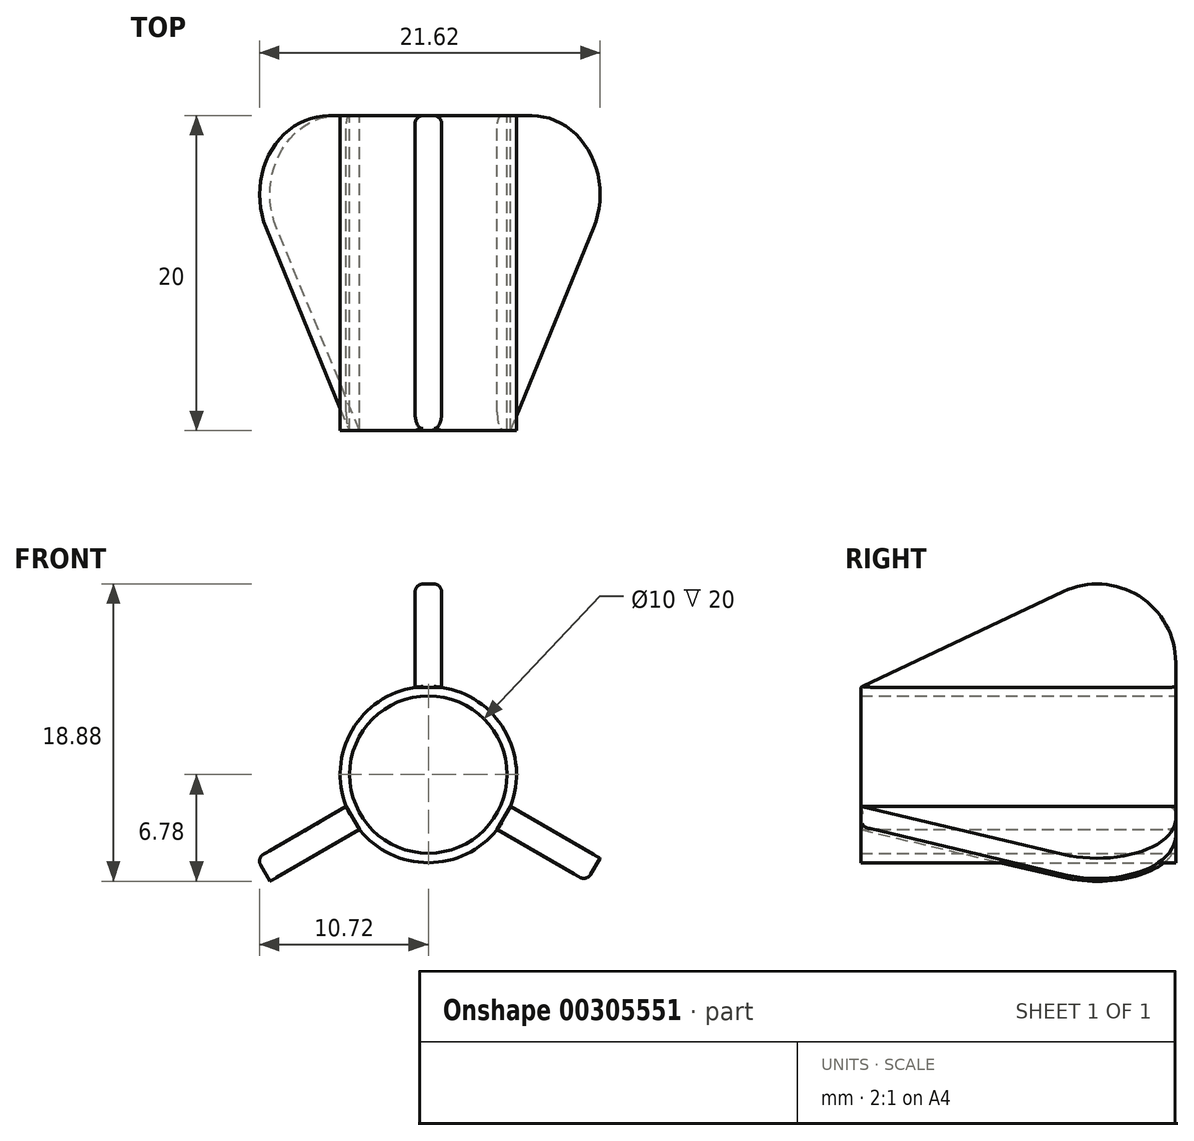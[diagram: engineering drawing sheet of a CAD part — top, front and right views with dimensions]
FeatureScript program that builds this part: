
annotation { "Feature Type Name" : "Feature", "Feature Type Description" : "" }
export const myFeature = defineFeature(function(context is Context, id is Id, definition is map)
    precondition{}
    {
        {
            var Q0;
            Q0=qCreatedBy(makeId("Front.planeOp"),FACE);
            var sketch = newSketch(context, id + "F0", { "sketchPlane" : qUnion([Q0])});
            skCircle(sketch, "E0", {"center": v(0, 0) * mm, "radius": 5 * mm});
            skCircle(sketch, "E1.0", {"center": v(0, 0) * mm, "radius": 5.6 * mm});
            skLineSegment(sketch, "E2.bottom", {"start": v(0, 5) * mm, "end": v(0.85, 5) * mm});
            skLineSegment(sketch, "E2.top", {"start": v(0, 15) * mm, "end": v(0.85, 15) * mm});
            skLineSegment(sketch, "E2.left", {"start": v(0, 5) * mm, "end": v(0, 15) * mm});
            skLineSegment(sketch, "E2.right", {"start": v(0.85, 5) * mm, "end": v(0.85, 15) * mm});
            skLineSegment(sketch, "E3.MirrorCS", {"start": v(0, 15) * mm, "end": v(-0.85, 15) * mm});
            skLineSegment(sketch, "E4.MirrorCS", {"start": v(0, 5) * mm, "end": v(-0.85, 5) * mm});
            skLineSegment(sketch, "E5.MirrorCS", {"start": v(-0.85, 5) * mm, "end": v(-0.85, 15) * mm});
            skLineSegment(sketch, "E6.1.0", {"start": v(-3.9, -3.23) * mm, "end": v(-12.57, -8.23) * mm});
            skLineSegment(sketch, "E6.1.1", {"start": v(-4.75, -1.77) * mm, "end": v(-13.41, -6.77) * mm});
            skLineSegment(sketch, "E6.1.2", {"start": v(-4.33, -2.5) * mm, "end": v(-13, -7.5) * mm});
            skLineSegment(sketch, "E6.1.3", {"start": v(-4.33, -2.5) * mm, "end": v(-3.9, -3.23) * mm});
            skLineSegment(sketch, "E6.1.4", {"start": v(-13, -7.5) * mm, "end": v(-12.57, -8.23) * mm});
            skLineSegment(sketch, "E6.1.5", {"start": v(-13, -7.5) * mm, "end": v(-13.41, -6.77) * mm});
            skLineSegment(sketch, "E6.1.6", {"start": v(-4.33, -2.5) * mm, "end": v(-4.75, -1.77) * mm});
            skLineSegment(sketch, "E6.2.0", {"start": v(4.75, -1.77) * mm, "end": v(13.41, -6.77) * mm});
            skLineSegment(sketch, "E6.2.1", {"start": v(3.9, -3.23) * mm, "end": v(12.57, -8.23) * mm});
            skLineSegment(sketch, "E6.2.2", {"start": v(4.33, -2.5) * mm, "end": v(13, -7.5) * mm});
            skLineSegment(sketch, "E6.2.3", {"start": v(4.33, -2.5) * mm, "end": v(4.75, -1.77) * mm});
            skLineSegment(sketch, "E6.2.4", {"start": v(13, -7.5) * mm, "end": v(13.41, -6.77) * mm});
            skLineSegment(sketch, "E6.2.5", {"start": v(13, -7.5) * mm, "end": v(12.57, -8.23) * mm});
            skLineSegment(sketch, "E6.2.6", {"start": v(4.33, -2.5) * mm, "end": v(3.9, -3.23) * mm});
            skSolve(sketch);
        }
        {
            var Q0;
            {var subQ0=sQuery(id+"F0.wireOp",EDGE,"E4.MirrorCS");Q0=makeQuery(id+"F0.imprint","IMPRINT",FACE,{"disambiguationData":[TD([[makeQuery(id+"F0.imprint","IMPRINT",EDGE,{"derivedFrom":subQ0}),1.0]])]});}
            var Q1;
            {var subQ0=sQuery(id+"F0.wireOp",EDGE,"E6.1.3");Q1=makeQuery(id+"F0.imprint","IMPRINT",FACE,{"disambiguationData":[TD([[makeQuery(id+"F0.imprint","IMPRINT",EDGE,{"derivedFrom":subQ0}),1.0]])]});}
            var Q2;
            {var subQ5=sQuery(id+"F0.wireOp",EDGE,"E6.1.3");Q2=makeQuery(id+"F0.imprint","IMPRINT",FACE,{"disambiguationData":[TD([[makeQuery(id+"F0.imprint","IMPRINT",EDGE,{"derivedFrom":subQ5}),-1.0]])]});}
            var Q3;
            {var subQ5=sQuery(id+"F0.wireOp",EDGE,"E6.1.6");Q3=makeQuery(id+"F0.imprint","IMPRINT",FACE,{"disambiguationData":[TD([[makeQuery(id+"F0.imprint","IMPRINT",EDGE,{"derivedFrom":subQ5}),1.0]])]});}
            var Q4;
            {var subQ5=sQuery(id+"F0.wireOp",EDGE,"E6.2.6");Q4=makeQuery(id+"F0.imprint","IMPRINT",FACE,{"disambiguationData":[TD([[makeQuery(id+"F0.imprint","IMPRINT",EDGE,{"derivedFrom":subQ5}),1.0]])]});}
            var Q5;
            {var subQ5=sQuery(id+"F0.wireOp",EDGE,"E6.2.3");Q5=makeQuery(id+"F0.imprint","IMPRINT",FACE,{"disambiguationData":[TD([[makeQuery(id+"F0.imprint","IMPRINT",EDGE,{"derivedFrom":subQ5}),-1.0]])]});}
            var Q6;
            {var subQ1=sQuery(id+"F0.wireOp",EDGE,"E2.bottom");Q6=makeQuery(id+"F0.imprint","IMPRINT",FACE,{"disambiguationData":[TD([[makeQuery(id+"F0.imprint","IMPRINT",EDGE,{"derivedFrom":subQ1}),-1.0]])]});}
            var Q7;
            {var subQ5=sQuery(id+"F0.wireOp",EDGE,"E2.bottom");Q7=makeQuery(id+"F0.imprint","IMPRINT",FACE,{"disambiguationData":[TD([[makeQuery(id+"F0.imprint","IMPRINT",EDGE,{"derivedFrom":subQ5}),1.0]])]});}
            var Q8;
            {var subQ5=sQuery(id+"F0.wireOp",EDGE,"E4.MirrorCS");Q8=makeQuery(id+"F0.imprint","IMPRINT",FACE,{"disambiguationData":[TD([[makeQuery(id+"F0.imprint","IMPRINT",EDGE,{"derivedFrom":subQ5}),-1.0]])]});}
            extrude(context, id + "F1", {"entities" : qUnion([Q0, Q1, Q2, Q3, Q4, Q5, Q6, Q7, Q8]), "depth" : 20 * mm});
        }
        {
            var Q0;
            {var subQ5=sQuery(id+"F0.wireOp",EDGE,"E6.1.4");Q0=makeQuery(id+"F0.imprint","IMPRINT",FACE,{"disambiguationData":[TD([[makeQuery(id+"F0.imprint","IMPRINT",EDGE,{"derivedFrom":subQ5}),1.0]])]});}
            var Q1;
            {var subQ5=sQuery(id+"F0.wireOp",EDGE,"E6.1.5");Q1=makeQuery(id+"F0.imprint","IMPRINT",FACE,{"disambiguationData":[TD([[makeQuery(id+"F0.imprint","IMPRINT",EDGE,{"derivedFrom":subQ5}),-1.0]])]});}
            extrude(context, id + "F2", {"entities" : qUnion([Q0, Q1]), "operationType" : NewBodyOperationType.ADD, "depth" : 20 * mm});
        }
        {
            var Q0;
            Q0=makeQuery(id+"F2.opExtrude","SWEPT_FACE",FACE,{"disambiguationData":[OSD([sQuery(id+"F0.wireOp",EDGE,"E6.1.0")])]});
            var sketch = newSketch(context, id + "F3", { "sketchPlane" : qUnion([Q0])});
            skLineSegment(sketch, "E7", {"start": v(-5.54, 20) * mm, "end": v(-15, 0) * mm});
            skSolve(sketch);
        }
        {
            var Q0;
            Q0=makeQuery(id+"F3.imprint","IMPRINT",FACE,{"disambiguationData":[TD([[makeQuery(id+"F3.imprint","IMPRINT",EDGE,{"derivedFrom":sQuery(id+"F3.wireOp",EDGE,"E7")}),-1.0]])]});
            extrude(context, id + "F4", {"entities" : qUnion([Q0]), "operationType" : NewBodyOperationType.REMOVE, "oppositeDirection" : true, "depth" : 14.8 * mm});
        }
        {
            var Q0;
            {var subQ0=sQuery(id+"F0.wireOp",EDGE,"E6.1.4");Q0=makeQuery(id+"F4.boolean.opBoolean","MERGE",EDGE,{"derivedFrom":[makeQuery(id+"F2.opExtrude","CAP_EDGE",EDGE,{"disambiguationData":[OSD([subQ0,sQuery(id+"F0.wireOp",EDGE,"E6.1.5")])],"isStart":true}),makeQuery(id+"F4.opExtrude","SWEPT_EDGE",EDGE,{"disambiguationData":[OSD([sQuery(id+"F0.wireOp",EDGE,"E6.1.0"),subQ0,sQuery(id+"F3.wireOp",EDGE,"E7")])]})]});}
            fillet(context, id + "F5", {"entities" : qUnion([Q0]), "radius" : 5 * mm, "tangentPropagation" : true, "allowEdgeOverflow" : false});
        }
        {
            var Q0;
            {var subQ5=sQuery(id+"F0.wireOp",EDGE,"E3.MirrorCS");Q0=makeQuery(id+"F0.imprint","IMPRINT",FACE,{"disambiguationData":[TD([[makeQuery(id+"F0.imprint","IMPRINT",EDGE,{"derivedFrom":subQ5}),1.0]])]});}
            var Q1;
            {var subQ5=sQuery(id+"F0.wireOp",EDGE,"E2.top");Q1=makeQuery(id+"F0.imprint","IMPRINT",FACE,{"disambiguationData":[TD([[makeQuery(id+"F0.imprint","IMPRINT",EDGE,{"derivedFrom":subQ5}),-1.0]])]});}
            var Q2;
            {var subQ5=sQuery(id+"F0.wireOp",EDGE,"E6.2.4");Q2=makeQuery(id+"F0.imprint","IMPRINT",FACE,{"disambiguationData":[TD([[makeQuery(id+"F0.imprint","IMPRINT",EDGE,{"derivedFrom":subQ5}),1.0]])]});}
            var Q3;
            {var subQ5=sQuery(id+"F0.wireOp",EDGE,"E6.2.5");Q3=makeQuery(id+"F0.imprint","IMPRINT",FACE,{"disambiguationData":[TD([[makeQuery(id+"F0.imprint","IMPRINT",EDGE,{"derivedFrom":subQ5}),-1.0]])]});}
            extrude(context, id + "F6", {"entities" : qUnion([Q0, Q1, Q2, Q3]), "operationType" : NewBodyOperationType.ADD, "depth" : 20 * mm});
        }
        {
            var Q0;
            Q0=makeQuery(id+"F6.opExtrude","SWEPT_FACE",FACE,{"disambiguationData":[OSD([sQuery(id+"F0.wireOp",EDGE,"E6.2.0")])]});
            var sketch = newSketch(context, id + "F7", { "sketchPlane" : qUnion([Q0])});
            skLineSegment(sketch, "E8", {"start": v(5.54, -20) * mm, "end": v(15, 0) * mm});
            skSolve(sketch);
        }
        {
            var Q0;
            Q0=makeQuery(id+"F7.imprint","IMPRINT",FACE,{"disambiguationData":[TD([[makeQuery(id+"F7.imprint","IMPRINT",EDGE,{"derivedFrom":sQuery(id+"F7.wireOp",EDGE,"E8")}),-1.0]])]});
            extrude(context, id + "F8", {"entities" : qUnion([Q0]), "operationType" : NewBodyOperationType.REMOVE, "oppositeDirection" : true, "depth" : 25 * mm});
        }
        {
            var Q0;
            Q0=makeQuery(id+"F6.opExtrude","SWEPT_FACE",FACE,{"disambiguationData":[OSD([sQuery(id+"F0.wireOp",EDGE,"E2.right")])]});
            var sketch = newSketch(context, id + "F9", { "sketchPlane" : qUnion([Q0])});
            skLineSegment(sketch, "E9", {"start": v(-20, 5.54) * mm, "end": v(0, 15) * mm});
            skSolve(sketch);
        }
        {
            var Q0;
            Q0=makeQuery(id+"F9.imprint","IMPRINT",FACE,{"disambiguationData":[TD([[makeQuery(id+"F9.imprint","IMPRINT",EDGE,{"derivedFrom":sQuery(id+"F9.wireOp",EDGE,"E9")}),1.0]])]});
            extrude(context, id + "F10", {"entities" : qUnion([Q0]), "operationType" : NewBodyOperationType.REMOVE, "oppositeDirection" : true, "depth" : 25 * mm});
        }
        {
            var Q0;
            {var subQ0=sQuery(id+"F0.wireOp",EDGE,"E6.2.4");Q0=makeQuery(id+"F8.boolean.opBoolean","MERGE",EDGE,{"derivedFrom":[makeQuery(id+"F6.opExtrude","CAP_EDGE",EDGE,{"disambiguationData":[OSD([subQ0,sQuery(id+"F0.wireOp",EDGE,"E6.2.5")])],"isStart":true}),makeQuery(id+"F8.opExtrude","SWEPT_EDGE",EDGE,{"disambiguationData":[OSD([sQuery(id+"F0.wireOp",EDGE,"E6.2.0"),subQ0,sQuery(id+"F7.wireOp",EDGE,"E8")])]})]});}
            var Q1;
            {var subQ0=sQuery(id+"F0.wireOp",EDGE,"E2.top");Q1=makeQuery(id+"F10.boolean.opBoolean","MERGE",EDGE,{"derivedFrom":[makeQuery(id+"F6.opExtrude","CAP_EDGE",EDGE,{"disambiguationData":[OSD([subQ0,sQuery(id+"F0.wireOp",EDGE,"E3.MirrorCS")])],"isStart":true}),makeQuery(id+"F10.opExtrude","SWEPT_EDGE",EDGE,{"disambiguationData":[OSD([subQ0,sQuery(id+"F0.wireOp",EDGE,"E2.right"),sQuery(id+"F9.wireOp",EDGE,"E9")])]})]});}
            fillet(context, id + "F11", {"entities" : qUnion([Q0, Q1]), "radius" : 5 * mm, "tangentPropagation" : true, "allowEdgeOverflow" : false});
        }
        {
            var Q0;
            Q0=makeQuery(id+"F10.boolean.opBoolean","COPY",EDGE,{"derivedFrom":makeQuery(id+"F10.opExtrude","CAP_EDGE",EDGE,{"disambiguationData":[OSD([sQuery(id+"F9.wireOp",EDGE,"E9")])],"isStart":true})});
            var Q1;
            Q1=makeQuery(id+"F10.boolean.opBoolean","INTERSECT",EDGE,{"derivedFrom":[makeQuery(id+"F6.opExtrude","SWEPT_FACE",FACE,{"disambiguationData":[OSD([sQuery(id+"F0.wireOp",EDGE,"E5.MirrorCS")])]}),makeQuery(id+"F10.opExtrude","SWEPT_FACE",FACE,{"disambiguationData":[OSD([sQuery(id+"F9.wireOp",EDGE,"E9")])]})]});
            var Q2;
            {var subQ0=sQuery(id+"F0.wireOp",EDGE,"E2.right");var subQ1=sQuery(id+"F0.wireOp",EDGE,"E2.top");Q2=makeQuery(id+"F11.opFillet","BLEND_EDGE",EDGE,{"blendedFrom":[makeQuery(id+"F10.boolean.opBoolean","MERGE",EDGE,{"derivedFrom":[makeQuery(id+"F6.opExtrude","CAP_EDGE",EDGE,{"disambiguationData":[OSD([subQ1,sQuery(id+"F0.wireOp",EDGE,"E3.MirrorCS")])],"isStart":true}),makeQuery(id+"F10.opExtrude","SWEPT_EDGE",EDGE,{"disambiguationData":[OSD([subQ1,subQ0,sQuery(id+"F9.wireOp",EDGE,"E9")])]})]}),makeQuery(id+"F6.opExtrude","SWEPT_FACE",FACE,{"disambiguationData":[OSD([subQ0])]})],"blendedInto":[makeQuery(id+"F6.opExtrude","SWEPT_FACE",FACE,{"disambiguationData":[OSD([subQ0])]})]});}
            var Q3;
            {var subQ0=sQuery(id+"F0.wireOp",EDGE,"E2.top");Q3=makeQuery(id+"F11.opFillet","BLEND_EDGE",EDGE,{"blendedFrom":[makeQuery(id+"F10.boolean.opBoolean","MERGE",EDGE,{"derivedFrom":[makeQuery(id+"F6.opExtrude","CAP_EDGE",EDGE,{"disambiguationData":[OSD([subQ0,sQuery(id+"F0.wireOp",EDGE,"E3.MirrorCS")])],"isStart":true}),makeQuery(id+"F10.opExtrude","SWEPT_EDGE",EDGE,{"disambiguationData":[OSD([subQ0,sQuery(id+"F0.wireOp",EDGE,"E2.right"),sQuery(id+"F9.wireOp",EDGE,"E9")])]})]}),makeQuery(id+"F6.opExtrude","SWEPT_FACE",FACE,{"disambiguationData":[OSD([sQuery(id+"F0.wireOp",EDGE,"E5.MirrorCS")])]})],"blendedInto":[makeQuery(id+"F6.opExtrude","SWEPT_FACE",FACE,{"disambiguationData":[OSD([sQuery(id+"F0.wireOp",EDGE,"E5.MirrorCS")])]})]});}
            fillet(context, id + "F12", {"entities" : qUnion([Q0, Q1, Q2, Q3]), "radius" : 0.5 * mm, "tangentPropagation" : true, "allowEdgeOverflow" : false});
        }
        {
            var Q0;
            Q0=makeQuery(id+"F8.boolean.opBoolean","COPY",EDGE,{"derivedFrom":makeQuery(id+"F8.opExtrude","CAP_EDGE",EDGE,{"disambiguationData":[OSD([sQuery(id+"F7.wireOp",EDGE,"E8")])],"isStart":true})});
            var Q1;
            Q1=makeQuery(id+"F8.boolean.opBoolean","INTERSECT",EDGE,{"derivedFrom":[makeQuery(id+"F6.opExtrude","SWEPT_FACE",FACE,{"disambiguationData":[OSD([sQuery(id+"F0.wireOp",EDGE,"E6.2.1")])]}),makeQuery(id+"F8.opExtrude","SWEPT_FACE",FACE,{"disambiguationData":[OSD([sQuery(id+"F7.wireOp",EDGE,"E8")])]})]});
            var Q2;
            Q2=makeQuery(id+"F4.boolean.opBoolean","COPY",EDGE,{"derivedFrom":makeQuery(id+"F4.opExtrude","CAP_EDGE",EDGE,{"disambiguationData":[OSD([sQuery(id+"F3.wireOp",EDGE,"E7")])],"isStart":true})});
            var Q3;
            Q3=makeQuery(id+"F4.boolean.opBoolean","INTERSECT",EDGE,{"derivedFrom":[makeQuery(id+"F2.opExtrude","SWEPT_FACE",FACE,{"disambiguationData":[OSD([sQuery(id+"F0.wireOp",EDGE,"E6.1.1")])]}),makeQuery(id+"F4.opExtrude","SWEPT_FACE",FACE,{"disambiguationData":[OSD([sQuery(id+"F3.wireOp",EDGE,"E7")])]})]});
            fillet(context, id + "F13", {"entities" : qUnion([Q0, Q1, Q2, Q3]), "radius" : 0.5 * mm, "tangentPropagation" : true, "allowEdgeOverflow" : false});
        }
    });
